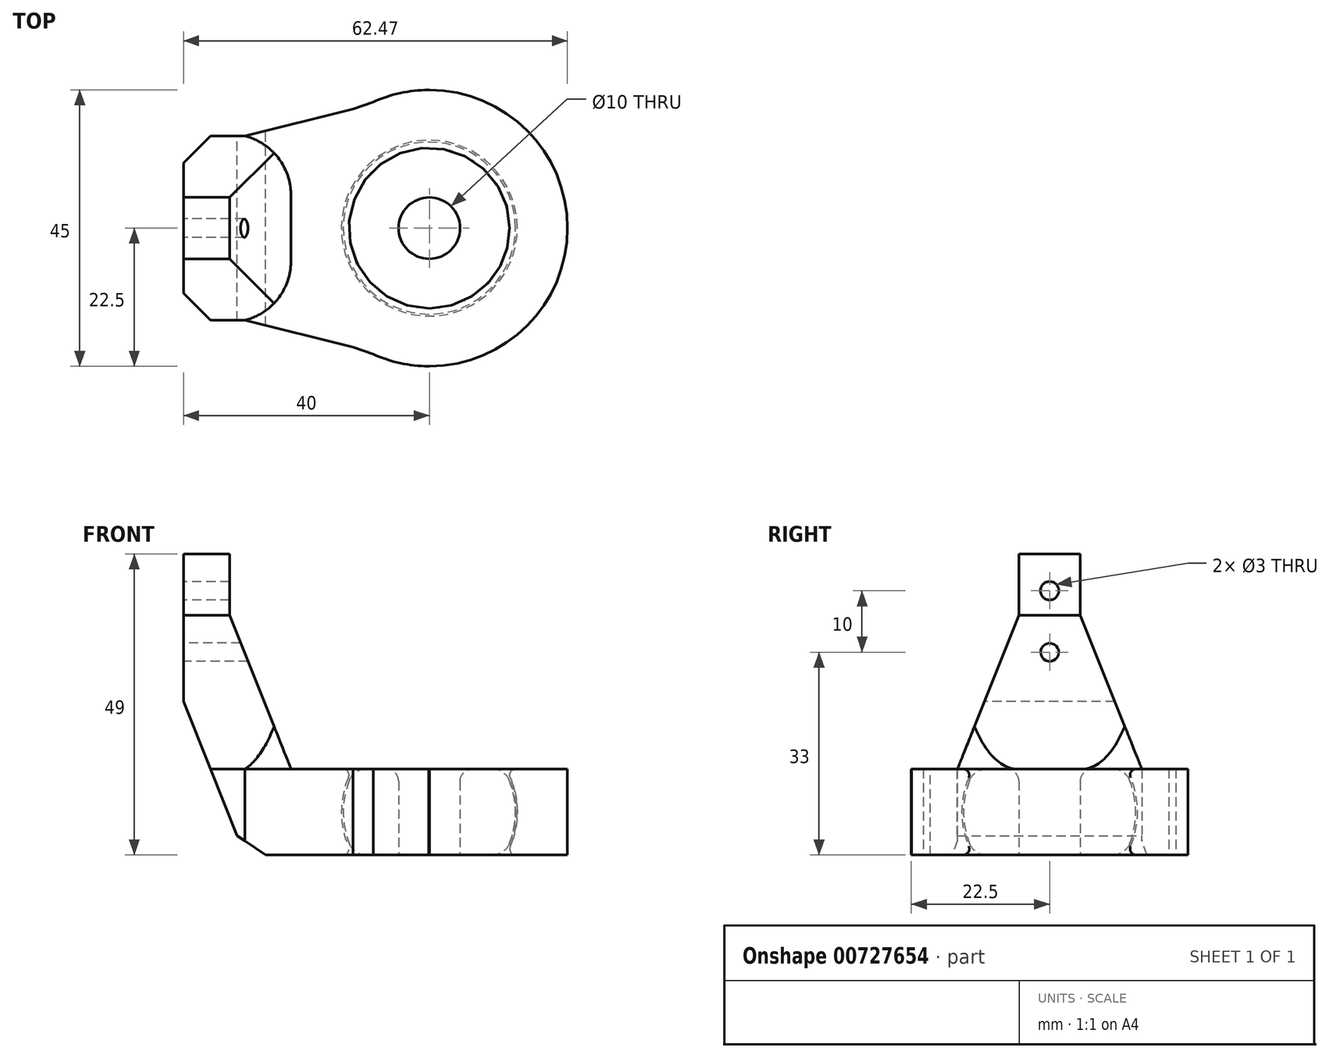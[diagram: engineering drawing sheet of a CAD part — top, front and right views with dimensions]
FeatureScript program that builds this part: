
annotation { "Feature Type Name" : "Feature", "Feature Type Description" : "" }
export const myFeature = defineFeature(function(context is Context, id is Id, definition is map)
    precondition{}
    {
        {
            var Q0;
            Q0=qCreatedBy(makeId("Front.planeOp"),FACE);
            var sketch = newSketch(context, id + "F0", { "sketchPlane" : qUnion([Q0])});
            skArc(sketch, "E0", {"start": v(12.12, 0) * mm, "mid": v(14, 7) * mm, "end": v(12.12, 14) * mm});
            skLineSegment(sketch, "E1", {"start": v(5, 14) * mm, "end": v(12.12, 14) * mm});
            skLineSegment(sketch, "E2", {"start": v(5, 0) * mm, "end": v(12.12, 0) * mm});
            skLineSegment(sketch, "E3", {"start": v(5, 0) * mm, "end": v(5, 14) * mm});
            skPoint(sketch, "E4.start.orphan", {"position": v(0, 0) * mm});
            skArc(sketch, "E5", {"start": v(12.47, 0) * mm, "mid": v(14.3, 7) * mm, "end": v(12.47, 14) * mm});
            skLineSegment(sketch, "E6", {"start": v(12.47, 14) * mm, "end": v(22.47, 14) * mm});
            skLineSegment(sketch, "E7", {"start": v(12.47, 0) * mm, "end": v(22.47, 0) * mm});
            skLineSegment(sketch, "E8", {"start": v(22.47, 14) * mm, "end": v(22.47, 0) * mm});
            skSolve(sketch);
        }
        {
            var Q0;
            Q0=qCreatedBy(makeId("Front.planeOp"),FACE);
            var sketch = newSketch(context, id + "F1", { "sketchPlane" : qUnion([Q0])});
            skLineSegment(sketch, "E9", {"start": v(0, 0) * mm, "end": v(0, 25.21) * mm});
            skSolve(sketch);
        }
        {
            var Q0;
            Q0=makeQuery(id+"F0.imprint","IMPRINT",FACE,{"disambiguationData":[TD([[makeQuery(id+"F0.imprint","IMPRINT",EDGE,{"derivedFrom":sQuery(id+"F0.wireOp",EDGE,"E0")}),1.0]])]});
            var Q1;
            Q1=makeQuery(id+"F0.imprint","IMPRINT",FACE,{"disambiguationData":[TD([[makeQuery(id+"F0.imprint","IMPRINT",EDGE,{"derivedFrom":sQuery(id+"F0.wireOp",EDGE,"E5")}),-1.0]])]});
            var Q2;
            Q2=sQuery(id+"F1.wireOp",EDGE,"E9");
            revolve(context, id + "F2", {"surfaceOperationType" : NewSurfaceOperationType.NEW, "entities" : qUnion([Q0, Q1]), "axis" : qUnion([Q2]), "revolveType" : RevolveType.FULL});
        }
        {
            var Q0;
            Q0=makeQuery(id+"F2.opRevolve","SWEPT_EDGE",EDGE,{"disambiguationData":[OSD([sQuery(id+"F0.wireOp",EDGE,"E0"),sQuery(id+"F0.wireOp",EDGE,"E1")])]});
            var Q1;
            Q1=makeQuery(id+"F2.opRevolve","SWEPT_EDGE",EDGE,{"disambiguationData":[OSD([sQuery(id+"F0.wireOp",EDGE,"E0"),sQuery(id+"F0.wireOp",EDGE,"E2")])]});
            fillet(context, id + "F3", {"entities" : qUnion([Q0, Q1]), "radius" : 3 * mm, "tangentPropagation" : true, "allowEdgeOverflow" : false});
        }
        {
            var Q0;
            Q0=makeQuery(id+"F2.opRevolve","SWEPT_EDGE",EDGE,{"disambiguationData":[OSD([sQuery(id+"F0.wireOp",EDGE,"E5"),sQuery(id+"F0.wireOp",EDGE,"E6")])]});
            var Q1;
            Q1=makeQuery(id+"F2.opRevolve","SWEPT_EDGE",EDGE,{"disambiguationData":[OSD([sQuery(id+"F0.wireOp",EDGE,"E5"),sQuery(id+"F0.wireOp",EDGE,"E7")])]});
            fillet(context, id + "F4", {"entities" : qUnion([Q0, Q1]), "radius" : 1 * mm, "tangentPropagation" : true, "allowEdgeOverflow" : false});
        }
        {
            var Q0;
            Q0=qCreatedBy(makeId("Top.planeOp"),FACE);
            var sketch = newSketch(context, id + "F5", { "sketchPlane" : qUnion([Q0])});
            skLineSegment(sketch, "E10", {"start": v(0, 19.22) * mm, "end": v(-15.75, 9.08) * mm});
            skLineSegment(sketch, "E11", {"start": v(-15.75, 9.08) * mm, "end": v(-15.75, -9.32) * mm});
            skLineSegment(sketch, "E12", {"start": v(-15.75, -9.32) * mm, "end": v(0, -18.87) * mm});
            skLineSegment(sketch, "E13", {"start": v(0, -18.87) * mm, "end": v(0, -22.5) * mm});
            skLineSegment(sketch, "E14", {"start": v(0, 22.5) * mm, "end": v(0, 19.22) * mm});
            skLineSegment(sketch, "E15", {"start": v(0, -22.5) * mm, "end": v(-30, -15) * mm});
            skLineSegment(sketch, "E16", {"start": v(-30, -15) * mm, "end": v(-30, 15) * mm});
            skLineSegment(sketch, "E17", {"start": v(-30, 15) * mm, "end": v(0, 22.5) * mm});
            skSolve(sketch);
        }
        {
            var Q0;
            Q0 = qSketchRegion(id + "F5", true);
            extrude(context, id + "F6", {"entities" : qUnion([Q0]), "operationType" : NewBodyOperationType.ADD, "depth" : 14 * mm, "offsetDistance" : 25 * mm});
        }
        {
            var Q0;
            Q0=makeQuery(id+"F6.boolean.opBoolean","INTERSECT",EDGE,{"disambiguationData":[OD(1.0)],"derivedFrom":[makeQuery(id+"F2.opRevolve","SWEPT_FACE",FACE,{"disambiguationData":[OSD([sQuery(id+"F0.wireOp",EDGE,"E8")])]}),makeQuery(id+"F6.opExtrude","SWEPT_FACE",FACE,{"disambiguationData":[OSD([sQuery(id+"F5.wireOp",EDGE,"E15")])]})]});
            var Q1;
            Q1=makeQuery(id+"F6.boolean.opBoolean","INTERSECT",EDGE,{"disambiguationData":[OD(1.0)],"derivedFrom":[makeQuery(id+"F2.opRevolve","SWEPT_FACE",FACE,{"disambiguationData":[OSD([sQuery(id+"F0.wireOp",EDGE,"E8")])]}),makeQuery(id+"F6.opExtrude","SWEPT_FACE",FACE,{"disambiguationData":[OSD([sQuery(id+"F5.wireOp",EDGE,"E17")])]})]});
            chamfer(context, id + "F7", {"entities" : qUnion([Q0, Q1]), "width" : 20 * mm, "tangentPropagation" : true});
        }
        {
            var Q0;
            Q0=makeQuery(id+"F6.opExtrude","SWEPT_FACE",FACE,{"disambiguationData":[OSD([sQuery(id+"F5.wireOp",EDGE,"E16")])]});
            extrude(context, id + "F8", {"entities" : qUnion([Q0]), "operationType" : NewBodyOperationType.ADD, "depth" : 10 * mm, "offsetDistance" : 25 * mm});
        }
        {
            var Q0;
            {var subQ0=sQuery(id+"F5.wireOp",EDGE,"E16");Q0=makeQuery(id+"F8.boolean.opBoolean","MERGE",FACE,{"derivedFrom":[makeQuery(id+"F6.boolean.opBoolean","MERGE",FACE,{"derivedFrom":[makeQuery(id+"F2.opRevolve","SWEPT_FACE",FACE,{"disambiguationData":[OSD([sQuery(id+"F0.wireOp",EDGE,"E6")])]}),makeQuery(id+"F6.opExtrude","CAP_FACE",FACE,{"disambiguationData":[OSD([sQuery(id+"F5.wireOp",EDGE,"E10"),sQuery(id+"F5.wireOp",EDGE,"E11"),sQuery(id+"F5.wireOp",EDGE,"E12"),sQuery(id+"F5.wireOp",EDGE,"E13"),sQuery(id+"F5.wireOp",EDGE,"E14"),sQuery(id+"F5.wireOp",EDGE,"E15"),subQ0,sQuery(id+"F5.wireOp",EDGE,"E17")])],"isStart":false})]}),makeQuery(id+"F8.opExtrude","SWEPT_FACE",FACE,{"disambiguationData":[OSD([subQ0]),TDD([makeQuery(id+"F6.opExtrude","CAP_EDGE",EDGE,{"disambiguationData":[OSD([subQ0])],"isStart":false})])]})]});}
            extrude(context, id + "F9", {"entities" : qUnion([Q0]), "operationType" : NewBodyOperationType.ADD, "depth" : 25 * mm, "offsetDistance" : 25 * mm});
        }
        {
            var Q0;
            Q0=qCreatedBy(makeId("Front.planeOp"),FACE);
            var sketch = newSketch(context, id + "F10", { "sketchPlane" : qUnion([Q0])});
            skLineSegment(sketch, "E18", {"start": v(27.5, 14) * mm, "end": v(-22.5, 14) * mm});
            skLineSegment(sketch, "E19", {"start": v(-22.5, 14) * mm, "end": v(-22.5, 114) * mm});
            skLineSegment(sketch, "E20", {"start": v(-22.5, 114) * mm, "end": v(27.5, 114) * mm});
            skLineSegment(sketch, "E21", {"start": v(27.5, 114) * mm, "end": v(27.5, 14) * mm});
            skSolve(sketch);
        }
        {
            var Q0;
            Q0=makeQuery(id+"F10.imprint","IMPRINT",FACE,{"disambiguationData":[TD([[makeQuery(id+"F10.imprint","IMPRINT",EDGE,{"derivedFrom":sQuery(id+"F10.wireOp",EDGE,"E18")}),-1.0]])]});
            extrude(context, id + "F11", {"entities" : qUnion([Q0]), "operationType" : NewBodyOperationType.REMOVE, "endBound" : BoundingType.SYMMETRIC, "oppositeDirection" : true, "depth" : 100 * mm, "offsetDistance" : 25 * mm});
        }
        {
            var Q0;
            {var subQ0=sQuery(id+"F5.wireOp",EDGE,"E15");var subQ1=makeQuery(id+"F6.opExtrude","SWEPT_FACE",FACE,{"disambiguationData":[OSD([subQ0])]});var subQ4=sQuery(id+"F5.wireOp",EDGE,"E16");var subQ12=makeQuery(id+"F6.opExtrude","SWEPT_FACE",FACE,{"disambiguationData":[OSD([subQ4])]});Q0=makeQuery(id+"F11.boolean.opBoolean","INTERSECT",EDGE,{"derivedFrom":[makeQuery(id+"F9.boolean.opBoolean","MERGE",FACE,{"derivedFrom":[makeQuery(id+"F6.boolean.opBoolean","SPLIT",FACE,{"disambiguationData":[TD([subQ12])],"derivedFrom":subQ1}),makeQuery(id+"F9.opExtrude","SWEPT_FACE",FACE,{"disambiguationData":[OSD([subQ0]),TDD([makeQuery(id+"F6.boolean.opBoolean","SPLIT",EDGE,{"disambiguationData":[TD([subQ12])],"derivedFrom":makeQuery(id+"F6.opExtrude","CAP_EDGE",EDGE,{"disambiguationData":[OSD([subQ0])],"isStart":false})})])]})]}),makeQuery(id+"F11.opExtrude","SWEPT_FACE",FACE,{"disambiguationData":[OSD([sQuery(id+"F10.wireOp",EDGE,"E19")])]})]});}
            var Q1;
            {var subQ0=sQuery(id+"F5.wireOp",EDGE,"E16");var subQ1=makeQuery(id+"F6.opExtrude","SWEPT_FACE",FACE,{"disambiguationData":[OSD([subQ0])]});var subQ2=sQuery(id+"F5.wireOp",EDGE,"E17");var subQ11=makeQuery(id+"F6.opExtrude","SWEPT_FACE",FACE,{"disambiguationData":[OSD([subQ2])]});Q1=makeQuery(id+"F11.boolean.opBoolean","INTERSECT",EDGE,{"derivedFrom":[makeQuery(id+"F9.boolean.opBoolean","MERGE",FACE,{"derivedFrom":[makeQuery(id+"F6.boolean.opBoolean","SPLIT",FACE,{"disambiguationData":[TD([subQ1])],"derivedFrom":subQ11}),makeQuery(id+"F9.opExtrude","SWEPT_FACE",FACE,{"disambiguationData":[OSD([subQ2]),TDD([makeQuery(id+"F6.boolean.opBoolean","SPLIT",EDGE,{"disambiguationData":[TD([subQ1])],"derivedFrom":makeQuery(id+"F6.opExtrude","CAP_EDGE",EDGE,{"disambiguationData":[OSD([subQ2])],"isStart":false})})])]})]}),makeQuery(id+"F11.opExtrude","SWEPT_FACE",FACE,{"disambiguationData":[OSD([sQuery(id+"F10.wireOp",EDGE,"E19")])]})]});}
            fillet(context, id + "F12", {"entities" : qUnion([Q0, Q1]), "radius" : 10 * mm, "tangentPropagation" : true, "allowEdgeOverflow" : false});
        }
        {
            var Q0;
            Q0=makeQuery(id+"F9.opExtrude","CAP_EDGE",EDGE,{"disambiguationData":[OSD([sQuery(id+"F5.wireOp",EDGE,"E15"),sQuery(id+"F5.wireOp",EDGE,"E16")])],"isStart":false});
            var Q1;
            Q1=makeQuery(id+"F9.opExtrude","CAP_EDGE",EDGE,{"disambiguationData":[OSD([sQuery(id+"F5.wireOp",EDGE,"E16"),sQuery(id+"F5.wireOp",EDGE,"E17")])],"isStart":false});
            chamfer(context, id + "F13", {"entities" : qUnion([Q0, Q1]), "chamferType" : ChamferType.TWO_OFFSETS, "width1" : 10 * mm, "oppositeDirection" : false, "width2" : 25 * mm, "tangentPropagation" : true});
        }
        {
            var Q0;
            Q0=makeQuery(id+"F11.boolean.opBoolean","INTERSECT",EDGE,{"derivedFrom":[makeQuery(id+"F9.opExtrude","CAP_FACE",FACE,{"disambiguationData":[OSD([sQuery(id+"F0.wireOp",EDGE,"E6"),sQuery(id+"F5.wireOp",EDGE,"E10"),sQuery(id+"F5.wireOp",EDGE,"E11"),sQuery(id+"F5.wireOp",EDGE,"E12"),sQuery(id+"F5.wireOp",EDGE,"E13"),sQuery(id+"F5.wireOp",EDGE,"E14"),sQuery(id+"F5.wireOp",EDGE,"E15"),sQuery(id+"F5.wireOp",EDGE,"E16"),sQuery(id+"F5.wireOp",EDGE,"E17")])],"isStart":false}),makeQuery(id+"F11.opExtrude","SWEPT_FACE",FACE,{"disambiguationData":[OSD([sQuery(id+"F10.wireOp",EDGE,"E19")])]})]});
            chamfer(context, id + "F14", {"entities" : qUnion([Q0]), "chamferType" : ChamferType.TWO_OFFSETS, "width1" : 25 * mm, "oppositeDirection" : false, "width2" : 10 * mm, "tangentPropagation" : true});
        }
        {
            var Q0;
            {var subQ0=sQuery(id+"F5.wireOp",EDGE,"E16");Q0=makeQuery(id+"F8.opExtrude","CAP_EDGE",EDGE,{"disambiguationData":[OSD([subQ0]),TDD([makeQuery(id+"F6.opExtrude","CAP_EDGE",EDGE,{"disambiguationData":[OSD([subQ0])],"isStart":true})])],"isStart":false});}
            chamfer(context, id + "F15", {"entities" : qUnion([Q0]), "chamferType" : ChamferType.TWO_OFFSETS, "width1" : 10 * mm, "oppositeDirection" : false, "width2" : 25 * mm, "tangentPropagation" : true});
        }
        {
            var Q0;
            {var subQ0=sQuery(id+"F5.wireOp",EDGE,"E16");var subQ1=makeQuery(id+"F6.opExtrude","CAP_EDGE",EDGE,{"disambiguationData":[OSD([subQ0])],"isStart":true});Q0=makeQuery(id+"F15.opChamfer","BLEND_EDGE",EDGE,{"blendedFrom":[makeQuery(id+"F8.opExtrude","CAP_EDGE",EDGE,{"disambiguationData":[OSD([subQ0]),TDD([subQ1])],"isStart":false}),makeQuery(id+"F8.boolean.opBoolean","MERGE",FACE,{"derivedFrom":[makeQuery(id+"F6.boolean.opBoolean","MERGE",FACE,{"derivedFrom":[makeQuery(id+"F2.opRevolve","SWEPT_FACE",FACE,{"disambiguationData":[OSD([sQuery(id+"F0.wireOp",EDGE,"E7")])]}),makeQuery(id+"F6.opExtrude","CAP_FACE",FACE,{"disambiguationData":[OSD([sQuery(id+"F5.wireOp",EDGE,"E10"),sQuery(id+"F5.wireOp",EDGE,"E11"),sQuery(id+"F5.wireOp",EDGE,"E12"),sQuery(id+"F5.wireOp",EDGE,"E13"),sQuery(id+"F5.wireOp",EDGE,"E14"),sQuery(id+"F5.wireOp",EDGE,"E15"),subQ0,sQuery(id+"F5.wireOp",EDGE,"E17")])],"isStart":true})]}),makeQuery(id+"F8.opExtrude","SWEPT_FACE",FACE,{"disambiguationData":[OSD([subQ0]),TDD([subQ1])]})]})],"blendedInto":[makeQuery(id+"F8.boolean.opBoolean","MERGE",FACE,{"derivedFrom":[makeQuery(id+"F6.boolean.opBoolean","MERGE",FACE,{"derivedFrom":[makeQuery(id+"F2.opRevolve","SWEPT_FACE",FACE,{"disambiguationData":[OSD([sQuery(id+"F0.wireOp",EDGE,"E7")])]}),makeQuery(id+"F6.opExtrude","CAP_FACE",FACE,{"disambiguationData":[OSD([sQuery(id+"F5.wireOp",EDGE,"E10"),sQuery(id+"F5.wireOp",EDGE,"E11"),sQuery(id+"F5.wireOp",EDGE,"E12"),sQuery(id+"F5.wireOp",EDGE,"E13"),sQuery(id+"F5.wireOp",EDGE,"E14"),sQuery(id+"F5.wireOp",EDGE,"E15"),subQ0,sQuery(id+"F5.wireOp",EDGE,"E17")])],"isStart":true})]}),makeQuery(id+"F8.opExtrude","SWEPT_FACE",FACE,{"disambiguationData":[OSD([subQ0]),TDD([subQ1])]})]})]});}
            chamfer(context, id + "F16", {"entities" : qUnion([Q0]), "width" : 5 * mm, "tangentPropagation" : true});
        }
        {
            var Q0;
            Q0=makeQuery(id+"F9.opExtrude","CAP_FACE",FACE,{"disambiguationData":[OSD([sQuery(id+"F0.wireOp",EDGE,"E6"),sQuery(id+"F5.wireOp",EDGE,"E10"),sQuery(id+"F5.wireOp",EDGE,"E11"),sQuery(id+"F5.wireOp",EDGE,"E12"),sQuery(id+"F5.wireOp",EDGE,"E13"),sQuery(id+"F5.wireOp",EDGE,"E14"),sQuery(id+"F5.wireOp",EDGE,"E15"),sQuery(id+"F5.wireOp",EDGE,"E16"),sQuery(id+"F5.wireOp",EDGE,"E17")])],"isStart":false});
            extrude(context, id + "F17", {"entities" : qUnion([Q0]), "operationType" : NewBodyOperationType.ADD, "depth" : 10 * mm, "offsetDistance" : 25 * mm});
        }
        {
            var Q0;
            {var subQ0=sQuery(id+"F5.wireOp",EDGE,"E16");Q0=makeQuery(id+"F17.boolean.opBoolean","MERGE",FACE,{"derivedFrom":[makeQuery(id+"F9.boolean.opBoolean","MERGE",FACE,{"derivedFrom":[makeQuery(id+"F8.opExtrude","CAP_FACE",FACE,{"disambiguationData":[OSD([subQ0])],"isStart":false}),makeQuery(id+"F9.opExtrude","SWEPT_FACE",FACE,{"disambiguationData":[OSD([subQ0])]})]}),makeQuery(id+"F17.opExtrude","SWEPT_FACE",FACE,{"disambiguationData":[OSD([subQ0])]})]});}
            var sketch = newSketch(context, id + "F18", { "sketchPlane" : qUnion([Q0])});
            skCircle(sketch, "E22", {"center": v(0, 33) * mm, "radius": 1.5 * mm});
            skCircle(sketch, "E23", {"center": v(0, 43) * mm, "radius": 1.5 * mm});
            skSolve(sketch);
        }
        {
            var Q0;
            Q0 = qSketchRegion(id + "F18", true);
            extrude(context, id + "F19", {"entities" : qUnion([Q0]), "operationType" : NewBodyOperationType.REMOVE, "oppositeDirection" : true, "depth" : 25 * mm, "offsetDistance" : 25 * mm});
        }
        {
            var Q0;
            Q0=makeQuery(id+"F2.opRevolve","SWEPT_EDGE",EDGE,{"disambiguationData":[OSD([sQuery(id+"F0.wireOp",EDGE,"E1"),sQuery(id+"F0.wireOp",EDGE,"E3")])]});
            fillet(context, id + "F20", {"entities" : qUnion([Q0]), "radius" : 2 * mm, "tangentPropagation" : true, "allowEdgeOverflow" : false});
        }
    });
